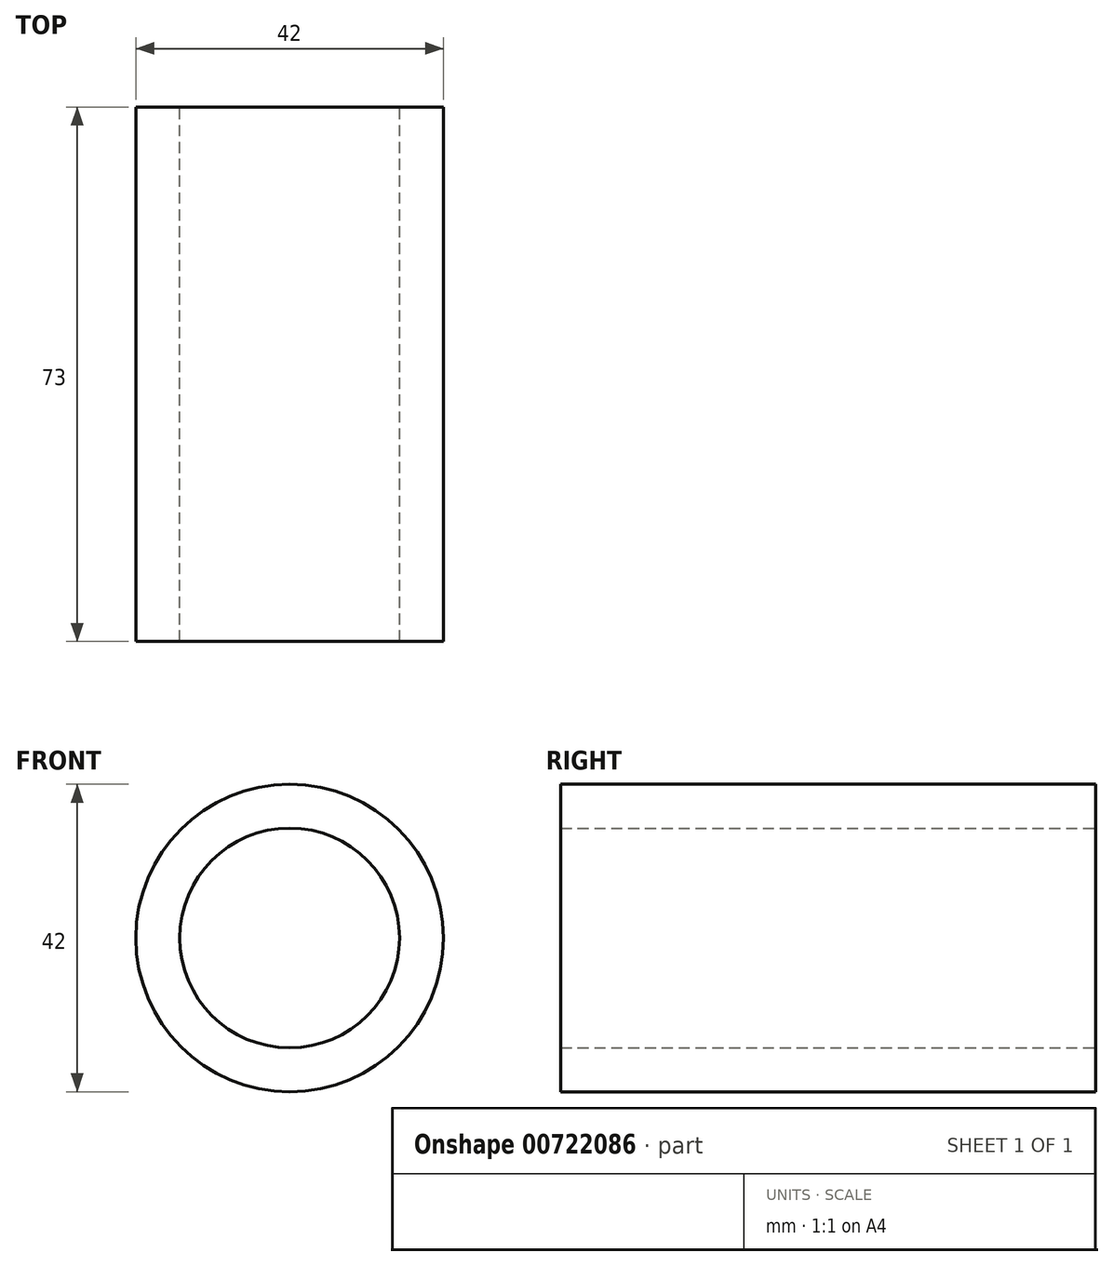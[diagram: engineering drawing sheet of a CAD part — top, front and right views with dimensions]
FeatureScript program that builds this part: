
annotation { "Feature Type Name" : "Feature", "Feature Type Description" : "" }
export const myFeature = defineFeature(function(context is Context, id is Id, definition is map)
    precondition{}
    {
        {
            var Q0;
            Q0=qCreatedBy(makeId("Front.planeOp"),FACE);
            var sketch = newSketch(context, id + "F0", { "sketchPlane" : qUnion([Q0])});
            skCircle(sketch, "E0", {"center": v(0, 0) * mm, "radius": 21 * mm});
            skCircle(sketch, "E1", {"center": v(0, 0) * mm, "radius": 15 * mm});
            skSolve(sketch);
        }
        {
            var Q0;
            Q0 = qSketchRegion(id + "F0", true);
            extrude(context, id + "F1", {"entities" : qUnion([Q0]), "depth" : 73 * mm, "offsetDistance" : 25 * mm});
        }
    });
